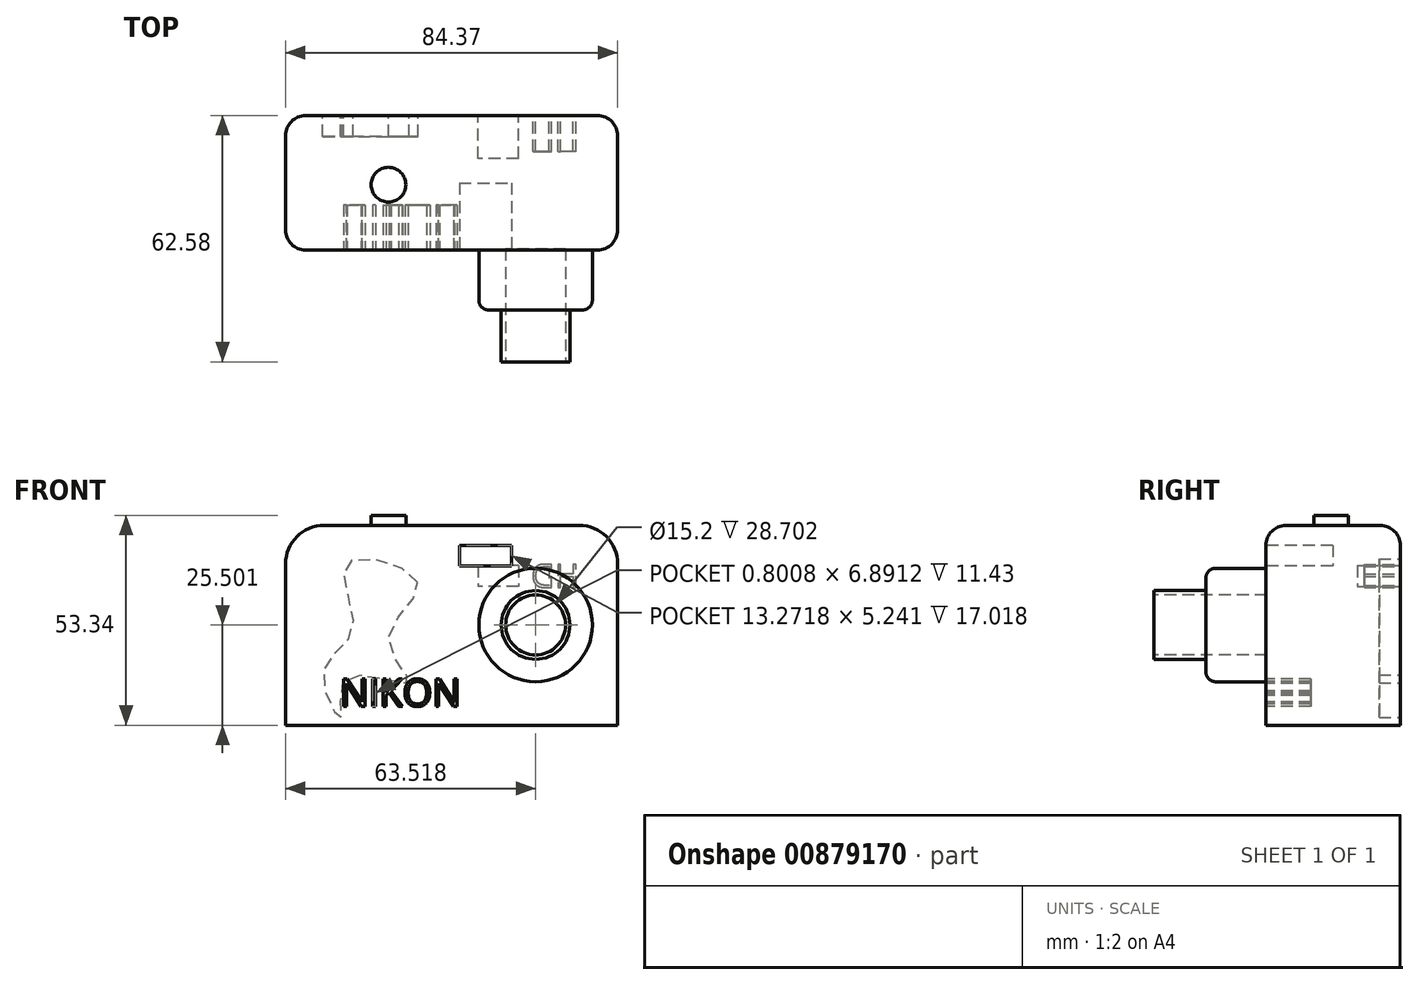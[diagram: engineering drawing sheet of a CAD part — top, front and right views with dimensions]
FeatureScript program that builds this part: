
annotation { "Feature Type Name" : "Feature", "Feature Type Description" : "" }
export const myFeature = defineFeature(function(context is Context, id is Id, definition is map)
    precondition{}
    {
        {
            var Q0;
            Q0=qCreatedBy(makeId("Top.planeOp"),FACE);
            var sketch = newSketch(context, id + "F0", { "sketchPlane" : qUnion([Q0])});
            skLineSegment(sketch, "E0.bottom", {"start": v(-41.24, 17.54) * mm, "end": v(43.13, 17.54) * mm});
            skLineSegment(sketch, "E0.top", {"start": v(-41.24, -16.59) * mm, "end": v(43.13, -16.59) * mm});
            skLineSegment(sketch, "E0.left", {"start": v(-41.24, 17.54) * mm, "end": v(-41.24, -16.59) * mm});
            skLineSegment(sketch, "E0.right", {"start": v(43.13, 17.54) * mm, "end": v(43.13, -16.59) * mm});
            skSolve(sketch);
        }
        {
            var Q0;
            Q0=makeQuery(id+"F0.imprint","IMPRINT",FACE,{"disambiguationData":[TD([[makeQuery(id+"F0.imprint","IMPRINT",EDGE,{"derivedFrom":sQuery(id+"F0.wireOp",EDGE,"E0.bottom")}),-1.0]])]});
            extrude(context, id + "F1", {"entities" : qUnion([Q0]), "depth" : 50.8 * mm, "offsetDistance" : 25.4 * mm});
        }
        {
            var Q0;
            Q0=makeQuery(id+"F1.opExtrude","SWEPT_FACE",FACE,{"disambiguationData":[OSD([sQuery(id+"F0.wireOp",EDGE,"E0.top")])]});
            var sketch = newSketch(context, id + "F2", { "sketchPlane" : qUnion([Q0])});
            skCircle(sketch, "E1", {"center": v(22.28, 25.5) * mm, "radius": 14.42 * mm});
            skSolve(sketch);
        }
        {
            var Q0;
            Q0=makeQuery(id+"F2.imprint","IMPRINT",FACE,{"disambiguationData":[TD([[makeQuery(id+"F2.imprint","IMPRINT",EDGE,{"derivedFrom":sQuery(id+"F2.wireOp",EDGE,"E1")}),1.0]])]});
            extrude(context, id + "F3", {"entities" : qUnion([Q0]), "operationType" : NewBodyOperationType.ADD, "depth" : 15.24 * mm, "offsetDistance" : 25.4 * mm});
        }
        {
            var Q0;
            Q0=makeQuery(id+"F1.opExtrude","CAP_EDGE",EDGE,{"disambiguationData":[OSD([sQuery(id+"F0.wireOp",EDGE,"E0.left")])],"isStart":false});
            fillet(context, id + "F4", {"entities" : qUnion([Q0]), "radius" : 9.8 * mm, "tangentPropagation" : true, "allowEdgeOverflow" : false});
        }
        {
            var Q0;
            Q0=makeQuery(id+"F3.opExtrude","CAP_EDGE",EDGE,{"disambiguationData":[OSD([sQuery(id+"F2.wireOp",EDGE,"E1")])],"isStart":false});
            fillet(context, id + "F5", {"entities" : qUnion([Q0]), "radius" : 2.45 * mm, "tangentPropagation" : true, "allowEdgeOverflow" : false});
        }
        {
            var Q0;
            Q0=makeQuery(id+"F1.opExtrude","CAP_EDGE",EDGE,{"disambiguationData":[OSD([sQuery(id+"F0.wireOp",EDGE,"E0.right")])],"isStart":false});
            fillet(context, id + "F6", {"entities" : qUnion([Q0]), "radius" : 9.8 * mm, "tangentPropagation" : true, "allowEdgeOverflow" : false});
        }
        {
            var Q0;
            Q0=makeQuery(id+"F1.opExtrude","CAP_EDGE",EDGE,{"disambiguationData":[OSD([sQuery(id+"F0.wireOp",EDGE,"E0.top")])],"isStart":false});
            var Q1;
            Q1=makeQuery(id+"F1.opExtrude","CAP_EDGE",EDGE,{"disambiguationData":[OSD([sQuery(id+"F0.wireOp",EDGE,"E0.bottom")])],"isStart":false});
            fillet(context, id + "F7", {"entities" : qUnion([Q0, Q1]), "radius" : 5.08 * mm, "tangentPropagation" : true, "allowEdgeOverflow" : false});
        }
        {
            var Q0;
            Q0=makeQuery(id+"F1.opExtrude","SWEPT_FACE",FACE,{"disambiguationData":[OSD([sQuery(id+"F0.wireOp",EDGE,"E0.top")])]});
            var sketch = newSketch(context, id + "F8", { "sketchPlane" : qUnion([Q0])});
            skText(sketch, "E2", { "text": "NIKON", "fontName": "OpenSans-Regular.ttf"});
            const initialGuessF8  = {"E2": [-0.03397, 0.0042, 1, 0, 0.00778]};
            skSetInitialGuess(sketch, initialGuessF8);
            skSolve(sketch);
        }
        {
            var Q0;
            Q0 = qSketchRegion(id + "F8", true);
            extrude(context, id + "F9", {"entities" : qUnion([Q0]), "operationType" : NewBodyOperationType.ADD, "oppositeDirection" : true, "depth" : 19.3 * mm, "offsetDistance" : 25.4 * mm});
        }
        {
            var Q0;
            Q0=makeQuery(id+"F1.opExtrude","SWEPT_FACE",FACE,{"disambiguationData":[OSD([sQuery(id+"F0.wireOp",EDGE,"E0.top")])]});
            var sketch = newSketch(context, id + "F10", { "sketchPlane" : qUnion([Q0])});
            skText(sketch, "E3", { "text": "Camera", "fontName": "OpenSans-Regular.ttf"});
            const initialGuessF10  = {"E3": [-0.03327, 0.00275, 1, 0, 0.00948]};
            skSetInitialGuess(sketch, initialGuessF10);
            skSolve(sketch);
        }
        {
            var Q0;
            Q0 = qSketchRegion(id + "F10", true);
            extrude(context, id + "F11", {"entities" : qUnion([Q0]), "operationType" : NewBodyOperationType.ADD, "oppositeDirection" : true, "depth" : 20.57 * mm, "offsetDistance" : 25.4 * mm});
        }
        {
            var Q0;
            Q0=makeQuery(id+"F1.opExtrude","SWEPT_FACE",FACE,{"disambiguationData":[OSD([sQuery(id+"F0.wireOp",EDGE,"E0.top")])]});
            var sketch = newSketch(context, id + "F12", { "sketchPlane" : qUnion([Q0])});
            skText(sketch, "E4", { "text": "NIKON", "fontName": "OpenSans-Regular.ttf"});
            const initialGuessF12  = {"E4": [-0.02741, 0.00484, 1, 0, 0.00695]};
            skSetInitialGuess(sketch, initialGuessF12);
            skSolve(sketch);
        }
        {
            var Q0;
            Q0 = qSketchRegion(id + "F12", true);
            extrude(context, id + "F13", {"entities" : qUnion([Q0]), "operationType" : NewBodyOperationType.REMOVE, "oppositeDirection" : true, "depth" : 11.43 * mm, "offsetDistance" : 25.4 * mm});
        }
        {
            var Q0;
            Q0=makeQuery(id+"F3.opExtrude","CAP_FACE",FACE,{"disambiguationData":[OSD([sQuery(id+"F2.wireOp",EDGE,"E1")])],"isStart":false});
            var sketch = newSketch(context, id + "F14", { "sketchPlane" : qUnion([Q0])});
            skCircle(sketch, "E5", {"center": v(22.28, 25.5) * mm, "radius": 8.74 * mm});
            skSolve(sketch);
        }
        {
            var Q0;
            Q0=makeQuery(id+"F14.imprint","IMPRINT",FACE,{"disambiguationData":[TD([[makeQuery(id+"F14.imprint","IMPRINT",EDGE,{"derivedFrom":sQuery(id+"F14.wireOp",EDGE,"E5")}),1.0]])]});
            extrude(context, id + "F15", {"entities" : qUnion([Q0]), "operationType" : NewBodyOperationType.ADD, "depth" : 13.2 * mm, "offsetDistance" : 25.4 * mm});
        }
        {
            var Q0;
            Q0=makeQuery(id+"F15.opExtrude","CAP_FACE",FACE,{"disambiguationData":[OSD([sQuery(id+"F14.wireOp",EDGE,"E5")])],"isStart":false});
            var sketch = newSketch(context, id + "F16", { "sketchPlane" : qUnion([Q0])});
            skCircle(sketch, "E6", {"center": v(22.28, 25.5) * mm, "radius": 7.6 * mm});
            skSolve(sketch);
        }
        {
            var Q0;
            Q0 = qSketchRegion(id + "F16", true);
            extrude(context, id + "F17", {"entities" : qUnion([Q0]), "operationType" : NewBodyOperationType.REMOVE, "oppositeDirection" : true, "depth" : 28.7 * mm, "offsetDistance" : 25.4 * mm});
        }
        {
            var Q0;
            Q0=makeQuery(id+"F1.opExtrude","CAP_FACE",FACE,{"disambiguationData":[OSD([sQuery(id+"F0.wireOp",EDGE,"E0.bottom"),sQuery(id+"F0.wireOp",EDGE,"E0.top"),sQuery(id+"F0.wireOp",EDGE,"E0.left"),sQuery(id+"F0.wireOp",EDGE,"E0.right")])],"isStart":false});
            var sketch = newSketch(context, id + "F18", { "sketchPlane" : qUnion([Q0])});
            skCircle(sketch, "E7", {"center": v(-15.07, 0) * mm, "radius": 4.41 * mm});
            skSolve(sketch);
        }
        {
            var Q0;
            Q0 = qSketchRegion(id + "F18", true);
            extrude(context, id + "F19", {"entities" : qUnion([Q0]), "operationType" : NewBodyOperationType.ADD, "depth" : 2.54 * mm, "offsetDistance" : 25.4 * mm});
        }
        {
            var Q0;
            {var subQ1=sQuery(id+"F0.wireOp",EDGE,"E0.top");var subQ3=makeQuery(id+"F1.opExtrude","SWEPT_FACE",FACE,{"disambiguationData":[OSD([subQ1])]});var subQ4=subQ3;Q0=makeQuery(id+"F13.boolean.opBoolean","SPLIT",FACE,{"disambiguationData":[TD([makeQuery(id+"F3.opExtrude","SWEPT_FACE",FACE,{"disambiguationData":[OSD([sQuery(id+"F2.wireOp",EDGE,"E1")])]})])],"derivedFrom":subQ4});}
            var sketch = newSketch(context, id + "F20", { "sketchPlane" : qUnion([Q0])});
            skLineSegment(sketch, "E8.bottom", {"start": v(2.94, 45.72) * mm, "end": v(16.21, 45.72) * mm});
            skLineSegment(sketch, "E8.top", {"start": v(2.94, 40.48) * mm, "end": v(16.21, 40.48) * mm});
            skLineSegment(sketch, "E8.left", {"start": v(2.94, 45.72) * mm, "end": v(2.94, 40.48) * mm});
            skLineSegment(sketch, "E8.right", {"start": v(16.21, 45.72) * mm, "end": v(16.21, 40.48) * mm});
            skSolve(sketch);
        }
        {
            var Q0;
            Q0 = qSketchRegion(id + "F20", true);
            extrude(context, id + "F21", {"entities" : qUnion([Q0]), "operationType" : NewBodyOperationType.REMOVE, "oppositeDirection" : true, "depth" : 17.02 * mm, "offsetDistance" : 25.4 * mm});
        }
        {
            var Q0;
            Q0=makeQuery(id+"F1.opExtrude","SWEPT_FACE",FACE,{"disambiguationData":[OSD([sQuery(id+"F0.wireOp",EDGE,"E0.bottom")])]});
            var sketch = newSketch(context, id + "F22", { "sketchPlane" : qUnion([Q0])});
            skText(sketch, "E9", { "text": "HD", "fontName": "OpenSans-Regular.ttf"});
            const initialGuessF22  = {"E9": [-0.03332, 0.03498, 1, 0, 0.006]};
            skSetInitialGuess(sketch, initialGuessF22);
            skSolve(sketch);
        }
        {
            var Q0;
            Q0 = qSketchRegion(id + "F22", true);
            extrude(context, id + "F23", {"entities" : qUnion([Q0]), "operationType" : NewBodyOperationType.REMOVE, "oppositeDirection" : true, "depth" : 9.14 * mm, "offsetDistance" : 25.4 * mm});
        }
        {
            var Q0;
            {var subQ1=sQuery(id+"F0.wireOp",EDGE,"E0.bottom");var subQ3=makeQuery(id+"F1.opExtrude","SWEPT_FACE",FACE,{"disambiguationData":[OSD([subQ1])]});var subQ4=subQ3;Q0=makeQuery(id+"F23.boolean.opBoolean","SPLIT",FACE,{"disambiguationData":[TD([makeQuery(id+"F7.opFillet","BLEND_FACE",FACE,{"disambiguationData":[OSD([subQ1])]})])],"derivedFrom":subQ4});}
            var sketch = newSketch(context, id + "F24", { "sketchPlane" : qUnion([Q0])});
            skLineSegment(sketch, "E10.bottom", {"start": v(-17.96, 40.6) * mm, "end": v(-7.7, 40.6) * mm});
            skLineSegment(sketch, "E10.top", {"start": v(-17.96, 35.33) * mm, "end": v(-7.7, 35.33) * mm});
            skLineSegment(sketch, "E10.left", {"start": v(-17.96, 40.6) * mm, "end": v(-17.96, 35.33) * mm});
            skLineSegment(sketch, "E10.right", {"start": v(-7.7, 40.6) * mm, "end": v(-7.7, 35.33) * mm});
            skSolve(sketch);
        }
        {
            var Q0;
            Q0 = qSketchRegion(id + "F24", true);
            extrude(context, id + "F25", {"entities" : qUnion([Q0]), "operationType" : NewBodyOperationType.REMOVE, "oppositeDirection" : true, "depth" : 10.92 * mm, "offsetDistance" : 25.4 * mm});
        }
        {
            var Q0;
            {var subQ1=sQuery(id+"F0.wireOp",EDGE,"E0.bottom");var subQ3=makeQuery(id+"F1.opExtrude","SWEPT_FACE",FACE,{"disambiguationData":[OSD([subQ1])]});var subQ4=subQ3;Q0=makeQuery(id+"F23.boolean.opBoolean","SPLIT",FACE,{"disambiguationData":[TD([makeQuery(id+"F7.opFillet","BLEND_FACE",FACE,{"disambiguationData":[OSD([subQ1])]})])],"derivedFrom":subQ4});}
            var sketch = newSketch(context, id + "F26", { "sketchPlane" : qUnion([Q0])});
            skFitSpline(sketch, "E11", {"points": [v(7.68, 36.3) * mm, v(25.5, 41.24) * mm, v(24.17, 24.55) * mm, v(31.76, 13.18) * mm, v(27.2, 2) * mm, v(25.88, 11.85) * mm, v(9.95, 10.9) * mm, v(15.07, 21.9) * mm, v(7.68, 36.3) * mm]});
            skSolve(sketch);
        }
        {
            var Q0;
            Q0 = qSketchRegion(id + "F26", true);
            extrude(context, id + "F27", {"entities" : qUnion([Q0]), "operationType" : NewBodyOperationType.REMOVE, "oppositeDirection" : true, "depth" : 5.33 * mm, "offsetDistance" : 25.4 * mm});
        }
    });
